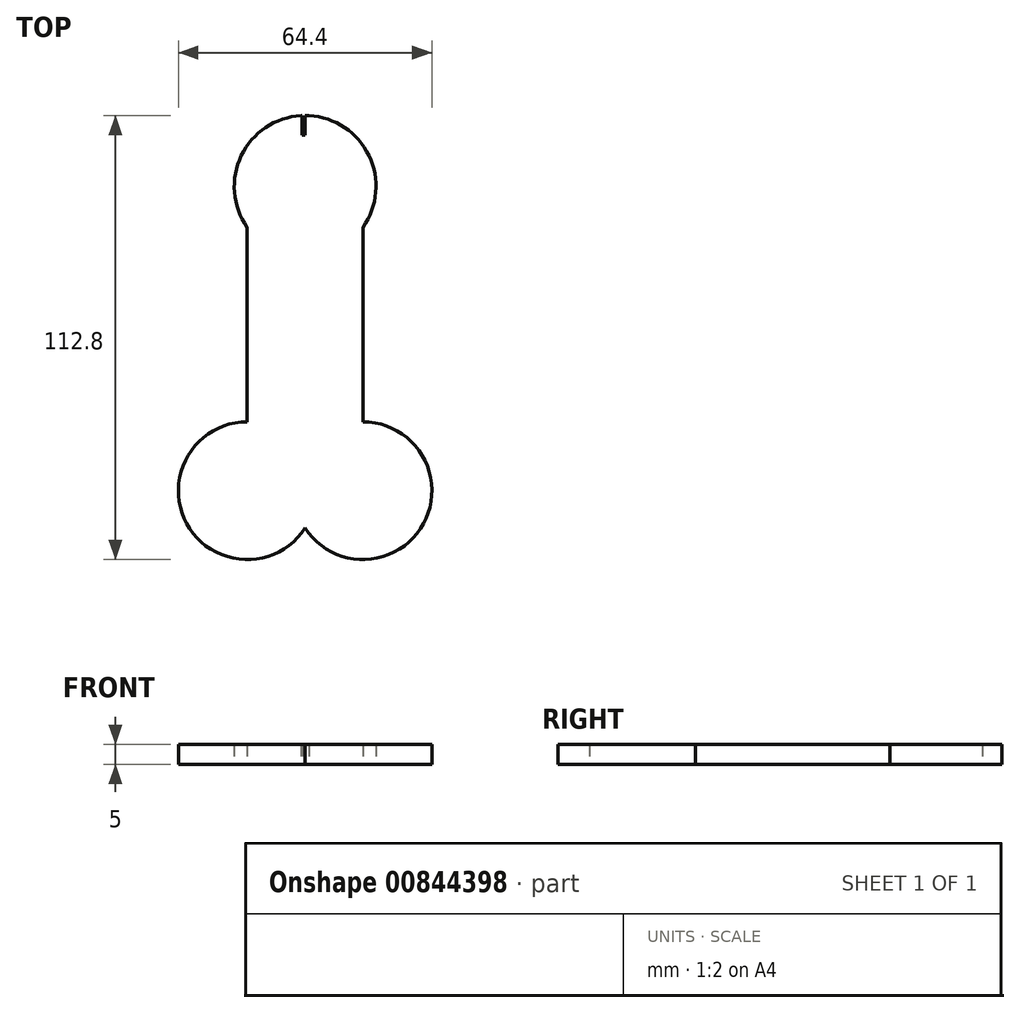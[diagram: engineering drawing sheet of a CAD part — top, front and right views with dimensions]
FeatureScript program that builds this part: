
annotation { "Feature Type Name" : "Feature", "Feature Type Description" : "" }
export const myFeature = defineFeature(function(context is Context, id is Id, definition is map)
    precondition{}
    {
        {
            var Q0;
            Q0=qCreatedBy(makeId("Top.planeOp"),FACE);
            var sketch = newSketch(context, id + "F0", { "sketchPlane" : qUnion([Q0])});
            skArc(sketch, "E0", {"start": v(14.7, 31.6) * mm, "mid": v(16, 50.28) * mm, "end": v(0, 60) * mm});
            skLineSegment(sketch, "E1", {"start": v(-14.7, 31.6) * mm, "end": v(-14.7, -17.82) * mm});
            skLineSegment(sketch, "E2", {"start": v(14.7, 31.6) * mm, "end": v(14.7, -17.82) * mm});
            skArc(sketch, "E3", {"start": v(-14.7, -17.82) * mm, "mid": v(-30.07, -43.7) * mm, "end": v(0, -44.81) * mm});
            skArc(sketch, "E4", {"start": v(0, -44.81) * mm, "mid": v(30.07, -43.7) * mm, "end": v(14.7, -17.82) * mm});
            skPoint(sketch, "E5.orphan", {"position": v(-14.7, -18.4) * mm});
            skPoint(sketch, "E6.orphan", {"position": v(14.7, -18.4) * mm});
            skLineSegment(sketch, "E7.top", {"start": v(-1.16, 59.98) * mm, "end": v(-0.77, 59.98) * mm});
            skLineSegment(sketch, "E8.top", {"start": v(0, 55) * mm, "end": v(-0.77, 55) * mm});
            skLineSegment(sketch, "E8.left", {"start": v(0, 60) * mm, "end": v(0, 55) * mm});
            skLineSegment(sketch, "E8.right", {"start": v(-0.77, 60) * mm, "end": v(-0.77, 55) * mm});
            skLineSegment(sketch, "E9.trimOffspring", {"start": v(0, 59.98) * mm, "end": v(1.04, 59.98) * mm});
            skArc(sketch, "E10.trimOffspring", {"start": v(-0.77, 59.99) * mm, "mid": v(-16.17, 49.93) * mm, "end": v(-14.7, 31.6) * mm});
            skPoint(sketch, "E11.center.orphan", {"position": v(0, -5.5) * mm});
            skSolve(sketch);
        }
        {
            var Q0;
            {var subQ10=sQuery(id+"F0.wireOp",EDGE,"E1");Q0=makeQuery(id+"F0.imprint","IMPRINT",FACE,{"disambiguationData":[TD([[makeQuery(id+"F0.imprint","IMPRINT",EDGE,{"derivedFrom":subQ10}),1.0]])]});}
            extrude(context, id + "F1", {"entities" : qUnion([Q0]), "depth" : 5 * mm, "offsetDistance" : 25 * mm});
        }
    });
